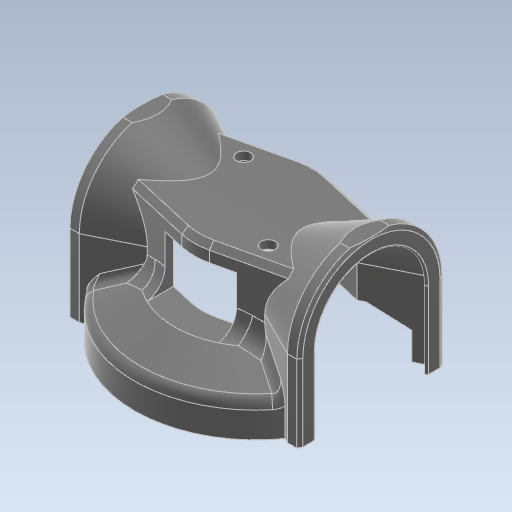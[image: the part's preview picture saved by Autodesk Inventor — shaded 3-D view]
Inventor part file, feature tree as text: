
AUTODESK INVENTOR PART (.ipt)
format: ipt  version: 2024 (Build 280153000, 153)  size: 545,280 bytes
history: native  units: mm
features: other x4, fillet x2, extrude x1, chamfer x1
ambient origin geometry x8: Origin, YZ Plane, XZ Plane, XY Plane, X Axis, Y Axis, Z Axis, Center Point
bodies: Body1 (feature_tree)
feature tree (8):
  other  "_bridseye_sketch.ipt"
  extrude  "押し出し2"  Depth=10.0mm
  chamfer  "面取り3"  Distance=4.0mm
  fillet  "フィレット2"  Radius=1.0mm
  fillet  "フィレット3"  [1 undecoded]
  other  "TaggingFeature1"
  other  "ソリッド13::_bridseye_sketch.ipt"
  other  "top_shoulderUnit-largeGearShaft_smallGearShaft"
note: 1 required parameter value undecoded (feature->parameter linkage not recoverable at this tier; creation-order binding heuristic only, values carry confidence <= 0.55)
